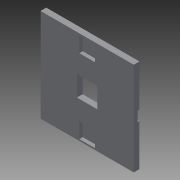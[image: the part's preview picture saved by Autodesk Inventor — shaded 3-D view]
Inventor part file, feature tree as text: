
AUTODESK INVENTOR PART (.ipt)
format: ipt  version: 2015 (Build 190159000, 159)  size: 220,160 bytes
history: native  units: mm
features: extrude x4, sketch x4, mirror x2
ambient origin geometry x8: Origin, YZ Plane, XZ Plane, XY Plane, X Axis, Y Axis, Z Axis, Center Point
bodies: Solid1 (feature_tree)
feature tree (10):
  extrude  "Extrusion1"  Depth=25.0mm
  extrude  "Extrusion2"  Depth=12.5mm
  extrude  "Extrusion3"  Depth=12.0mm
  extrude  "Extrusion4"  Depth=26.0mm
  mirror  "Mirror1"
  mirror  "Mirror2"
  sketch  "Sketch1"  dims[d2=25.0mm d3=25.0mm]
  sketch  "Sketch2"  dims[d4=12.5mm d5=12.5mm]
  sketch  "Sketch3"  dims[d6=6.0mm d7=12.0mm]
  sketch  "Sketch4"  dims[d8=26.0mm d9=26.0mm d10=6.0mm d11=12.0mm d12=19.1mm d13=19.1mm d14=9.55mm d15=19.1mm d16=19.1mm d17=9.55mm d22=0.0mm d23=0.0mm d24=2.0mm d25=2.0mm d26=114.3mm d28=57.15mm d29=57.15mm d30=114.3mm d37=28.575mm d38=28.575mm d39=6.4mm d40=6.4mm d41=6.4mm d43=120.0deg d44=120.0deg d45=32.127187mm d46=28.575mm d47=28.575mm d48=28.575mm d49=28.575mm d50=28.575mm d51=28.575mm d52=6.4mm d53=6.4mm d54=6.4mm d55=120.0deg d56=120.0deg d57=32.127187mm d58=6.4mm d59=6.4mm d60=6.4mm d61=120.0deg d62=120.0deg d63=32.127187mm d64=6.4mm d65=6.4mm d66=6.4mm d67=120.0deg d68=120.0deg d69=32.127187mm d70=7.0mm d71=0.0mm d72=2.0mm d73=0.0mm d74=4.65mm d75=0.0mm d76=2.84mm d77=0.0mm]
